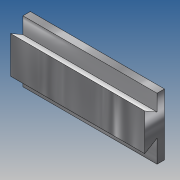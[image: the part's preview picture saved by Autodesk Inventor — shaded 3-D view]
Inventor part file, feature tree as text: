
AUTODESK INVENTOR PART (.ipt)
format: ipt  version: 2018.3 (Build 223284000, 284)  size: 145,408 bytes
history: native  units: in
note: dims shown in document units (in); Inventor stores cm internally (conversion verified against a paired STEP export)
features: extrude x4, sketch x3, mirror x1
ambient origin geometry x8: Origin, YZ Plane, XZ Plane, XY Plane, X Axis, Y Axis, Z Axis, Center Point
bodies: Solid1 (feature_tree)
feature tree (8):
  extrude  "Extrusion1"  Depth=0.134in
  extrude  "Extrusion2"  TaperAngle=60.0deg  [1 undecoded]
  mirror  "Mirror1"
  sketch  "Sketch5"  dims[d7=0.325in d8=0.0in d15=0.0222in d20=0.012in d22=0.175in d23=0.0in d28=0.0275in d29=0.015in d30=0.19in d31=0.0in d32=0.0448in d33=0.018in]
  extrude  "Extrusion5"  Depth=0.018in
  extrude  "Extrusion7"  Depth=0.012in
  sketch  "Sketch1"  dims[d0=0.325in d1=0.134in]
  sketch  "Sketch2"  dims[d2=0.048in d3=0.0in d6=60.0deg]
note: 1 required parameter value undecoded (feature->parameter linkage not recoverable at this tier; creation-order binding heuristic only, values carry confidence <= 0.55)
